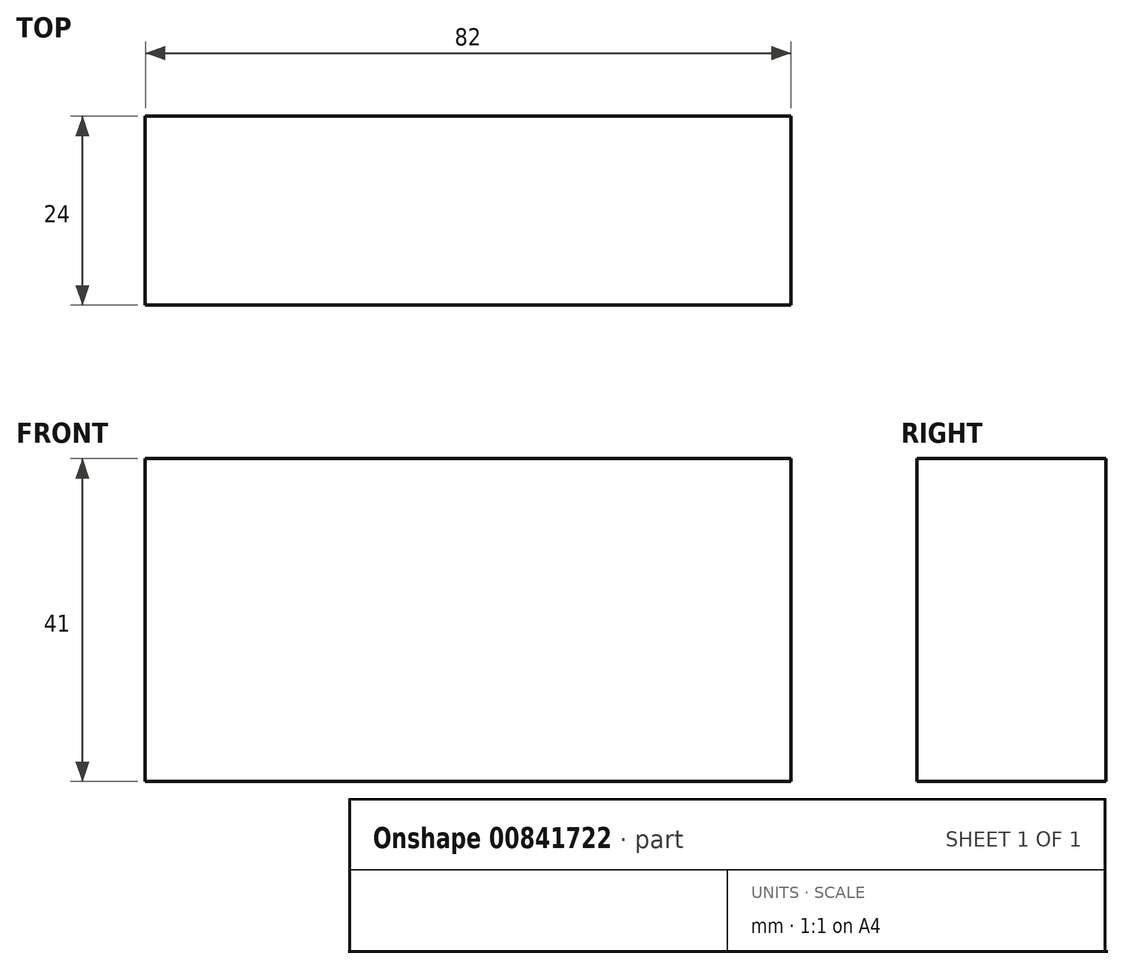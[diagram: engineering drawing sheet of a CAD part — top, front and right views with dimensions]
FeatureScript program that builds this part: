
annotation { "Feature Type Name" : "Feature", "Feature Type Description" : "" }
export const myFeature = defineFeature(function(context is Context, id is Id, definition is map)
    precondition{}
    {
        {
            var Q0;
            Q0=qCreatedBy(makeId("Front.planeOp"),FACE);
            var sketch = newSketch(context, id + "F0", { "sketchPlane" : qUnion([Q0])});
            skLineSegment(sketch, "E0.bottom", {"start": v(-33.1, 22.65) * mm, "end": v(48.9, 22.65) * mm});
            skLineSegment(sketch, "E0.top", {"start": v(-33.1, -18.35) * mm, "end": v(48.9, -18.35) * mm});
            skLineSegment(sketch, "E0.left", {"start": v(-33.1, 22.65) * mm, "end": v(-33.1, -18.35) * mm});
            skLineSegment(sketch, "E0.right", {"start": v(48.9, 22.65) * mm, "end": v(48.9, -18.35) * mm});
            skSolve(sketch);
        }
        {
            var Q0;
            Q0 = qSketchRegion(id + "F0", true);
            extrude(context, id + "F1", {"entities" : qUnion([Q0]), "endBound" : BoundingType.SYMMETRIC, "depth" : 24 * mm, "offsetDistance" : 25 * mm});
        }
    });
